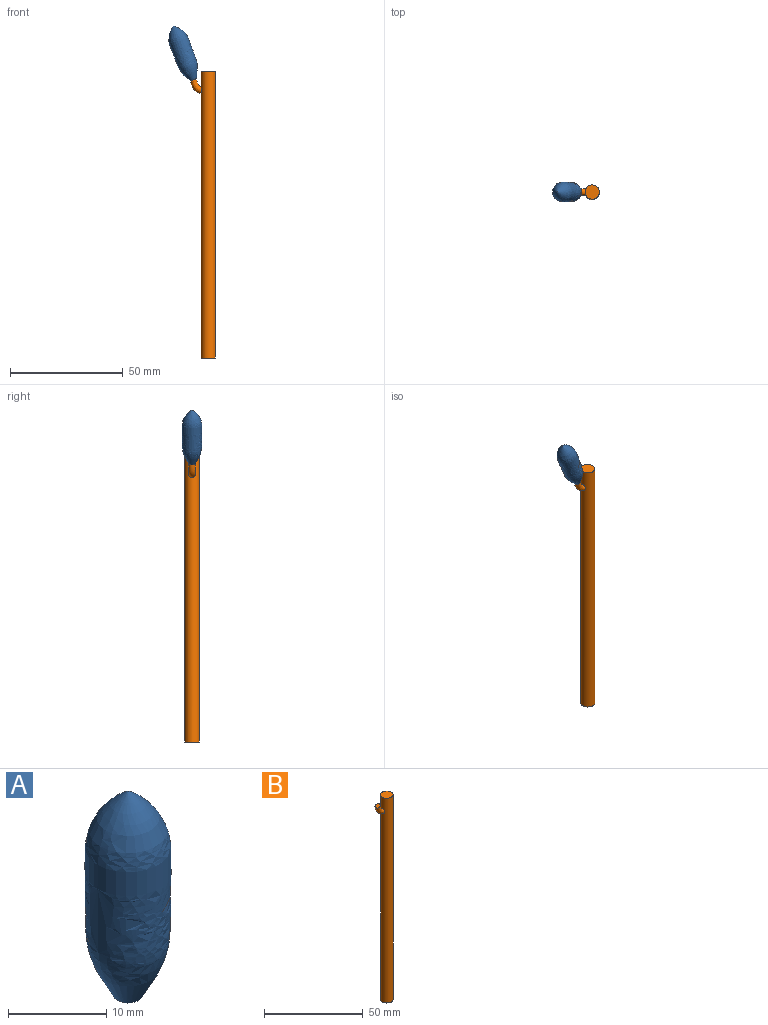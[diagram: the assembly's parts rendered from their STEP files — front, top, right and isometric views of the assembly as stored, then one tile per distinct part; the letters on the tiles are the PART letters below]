
ASSEMBLY  parts=2 mates=1
PART A: 2 faces, bbox 8.9x8.9x25.4 mm
  f0: revolved ~25.4x8.87mm, area 606.9mm2, adj f1
  f1: plane 2.95x2.95mm, normal (0,0,-1), area 6.8mm2, adj f0
PART B: 5 faces, bbox 11.4x6.7x127.4 mm
  f0: cylinder r=3.17mm len=127mm, axis (0,0,-1), area 2527.2mm2, adj f1,f2,f3
  f1: plane 6.35x6.35mm, normal (0,0,1), area 31.7mm2, adj f0
  f2: plane 6.35x6.35mm, normal (0,0,-1), area 31.7mm2, adj f0
  f3: bspline ~6.94x6.05mm, area 54.9mm2, adj f0,f4
  f4: plane 3.14x2.96mm, normal (-0.35,0,0.94), area 6mm2, adj f3
PLACE A rot(axis=(0,-1,0),20.7deg) t=(-24,19.15,105.59)mm
PLACE B t=(-17.44,19.15,-17.65)mm fixed
MATE fastened A.f1 <-> B.f4  axis (0.35,0,-0.94) through (-24,19.15,105.59)mm
